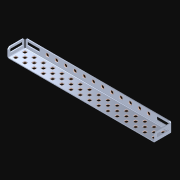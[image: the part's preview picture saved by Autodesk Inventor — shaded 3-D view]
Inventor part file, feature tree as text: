
AUTODESK INVENTOR PART (.ipt)
format: ipt  version: 2021 (Build 250183000, 183)  size: 1,003,520 bytes
history: native  units: in
note: dims shown in document units (in); Inventor stores cm internally (conversion verified against a paired STEP export)
features: other x60, extrude x59, pattern_linear x3, sketch x2, imported_body x1
ambient origin geometry x8: Origin, YZ Plane, XZ Plane, XY Plane, X Axis, Y Axis, Z Axis, Center Point
bodies: Body1 (feature_tree), Body2 (feature_tree), Body3 (feature_tree), Body4 (feature_tree), Body5 (feature_tree), Body6 (feature_tree), Body7 (feature_tree), Body8 (feature_tree), Body9 (feature_tree), Body10 (feature_tree), Body11 (feature_tree), Body12 (feature_tree), Body13 (feature_tree), Body14 (feature_tree), Body15 (feature_tree), Body16 (feature_tree), Body17 (feature_tree), Body18 (feature_tree), Body19 (feature_tree), Body20 (feature_tree), Body21 (feature_tree), Body22 (feature_tree), Body23 (feature_tree), Body24 (feature_tree), Body25 (feature_tree), Body26 (feature_tree), Body27 (feature_tree), Body28 (feature_tree), Body29 (feature_tree), Body30 (feature_tree), Body31 (feature_tree), Body32 (feature_tree), Body33 (feature_tree), Body34 (feature_tree), Body35 (feature_tree), Body36 (feature_tree), Body37 (feature_tree), Body38 (feature_tree), Body39 (feature_tree), Body40 (feature_tree), Body41 (feature_tree), Body42 (feature_tree), Body43 (feature_tree), Body44 (feature_tree), Body45 (feature_tree), Body46 (feature_tree), Body47 (feature_tree), Body48 (feature_tree), Body49 (feature_tree), Body50 (feature_tree), Body51 (feature_tree), Body52 (feature_tree), Body53 (feature_tree), Body54 (feature_tree), Body55 (feature_tree), Body56 (feature_tree), Body57 (feature_tree), Body58 (feature_tree), Body59 (feature_tree), Body60 (feature_tree)
feature tree (125):
  parser-record x1  (decoder bookkeeping rows leaked as tree rows — omitted from the tree; the rows remain in map.json)
  imported_body  "Base1"
  pattern_linear  "Rectangular Pattern1"  Count1=16 Spacing1=0.5in
  pattern_linear  "Rectangular Pattern2"  Count1=2 Spacing1=0.5in
  pattern_linear  "Rectangular Pattern3"  Count1=15 Spacing1=0.5in
  other  "Srf1"
  other  "Srf2"
  other  "Srf3"
  other  "Srf4"
  other  "Srf5"
  other  "Srf6"
  other  "Srf7"
  other  "Srf8"
  other  "Srf9"
  other  "Srf10"
  other  "Srf11"
  other  "Srf12"
  other  "Srf13"
  other  "Srf14"
  other  "Srf15"
  other  "Srf16"
  other  "Srf17"
  other  "Srf18"
  other  "Srf19"
  other  "Srf20"
  other  "Srf21"
  other  "Srf22"
  other  "Srf23"
  other  "Srf24"
  other  "Srf25"
  other  "Srf26"
  other  "Srf27"
  other  "Srf28"
  other  "Srf29"
  other  "Srf30"
  other  "Srf31"
  other  "Srf32"
  sketch  "Sketch10"  dims[d70=0.046in d71=0.0in d72=6.2992in d74=0.5in d75=0.7874in d77=0.5in]
  other  "Srf33"
  other  "Srf34"
  other  "Srf35"
  other  "Srf36"
  other  "Srf37"
  other  "Srf38"
  other  "Srf39"
  other  "Srf40"
  other  "Srf41"
  other  "Srf42"
  other  "Srf43"
  other  "Srf44"
  other  "Srf45"
  other  "Srf46"
  other  "Srf47"
  sketch  "Sketch11"  dims[d79=0.046in d80=0.0in d81=5.9055in d83=0.5in d85=0.046in d86=0.0in d87=4.7244in d89=0.5in d90=0.0in d91=0.0in d92=0.0in d93=0.0in d94=0.0in d95=0.0in d96=0.0in d97=0.0in d98=0.0in d99=0.0in d100=0.0in d101=0.0in d102=0.0in d103=0.0in d104=0.0in d105=0.0in d106=0.0in d107=0.0in d108=0.0in d109=0.0in d110=0.0in d111=0.0in d112=0.0in d113=0.0in d114=0.0in d115=0.0in d116=0.0in d117=0.0in d118=0.0in d119=0.0in d120=0.0in d121=0.0in d122=0.0in d123=0.0in d124=0.0in d125=0.0in d126=0.0in d127=0.0in d128=0.0in d129=0.0in d130=0.0in d131=0.0in d132=0.0in d133=0.0in d134=0.0in d135=0.0in d136=0.0in d137=0.0in d138=0.0in d139=0.0in d140=0.0in d141=0.0in d142=0.0in d143=0.0in d144=0.0in d145=0.0in d146=0.0in d147=0.0in d148=0.0in d149=0.0in d150=0.0in d151=0.0in d152=0.0in d153=0.0in d154=0.0in d155=0.0in d156=0.0in d157=0.0in d158=0.0in d159=0.0in d160=0.0in d161=0.0in d162=0.0in d163=0.0in d164=0.0in d165=0.0in d166=0.0in d167=0.0in d168=0.0in d169=0.0in d170=0.0in d171=0.0in d172=0.0in d173=0.0in d174=0.0in d175=0.0in d176=0.0in d177=0.0in d178=0.0in d179=0.0in d180=0.0in d181=0.0in d182=0.0in d183=0.0in d184=0.0in d185=0.0in d186=0.0in d187=0.0in d188=0.0in d189=0.0in d190=0.0in d191=0.0in d192=0.0in d193=0.0in d194=0.0in d195=0.0in d196=0.0in d197=0.0in d198=0.0in d199=0.0in d200=0.0in d201=0.0in d202=0.0in d203=0.0in d204=0.0in d205=0.0in d206=0.0in d207=0.0in]
  other  "Srf48"
  other  "Srf49"
  other  "Srf50"
  other  "Srf51"
  other  "Srf52"
  other  "Srf53"
  other  "Srf54"
  other  "Srf55"
  other  "Srf56"
  other  "Srf57"
  other  "Srf58"
  other  "Srf59"
  extrude  "ExtrusionSrf1"  Depth=0.046in TaperAngle=0.0deg
  extrude  "ExtrusionSrf33"  Depth=0.5in
  extrude  "ExtrusionSrf48"  [1 undecoded]
  extrude  "ExtrusionSrf2"  [1 undecoded]
  extrude  "ExtrusionSrf3"  [1 undecoded]
  extrude  "ExtrusionSrf4"  [1 undecoded]
  extrude  "ExtrusionSrf5"  [1 undecoded]
  extrude  "ExtrusionSrf6"  [1 undecoded]
  extrude  "ExtrusionSrf7"  [1 undecoded]
  extrude  "ExtrusionSrf8"  [1 undecoded]
  extrude  "ExtrusionSrf9"  [1 undecoded]
  extrude  "ExtrusionSrf10"  [1 undecoded]
  extrude  "ExtrusionSrf11"  [1 undecoded]
  extrude  "ExtrusionSrf12"  [1 undecoded]
  extrude  "ExtrusionSrf13"  [1 undecoded]
  extrude  "ExtrusionSrf14"  [1 undecoded]
  extrude  "ExtrusionSrf15"  [1 undecoded]
  extrude  "ExtrusionSrf16"  [1 undecoded]
  extrude  "ExtrusionSrf17"  [1 undecoded]
  extrude  "ExtrusionSrf18"  [1 undecoded]
  extrude  "ExtrusionSrf19"  [1 undecoded]
  extrude  "ExtrusionSrf20"  [1 undecoded]
  extrude  "ExtrusionSrf21"  [1 undecoded]
  extrude  "ExtrusionSrf22"  [1 undecoded]
  extrude  "ExtrusionSrf23"  [1 undecoded]
  extrude  "ExtrusionSrf24"  [1 undecoded]
  extrude  "ExtrusionSrf25"  [1 undecoded]
  extrude  "ExtrusionSrf26"  [1 undecoded]
  extrude  "ExtrusionSrf27"  [1 undecoded]
  extrude  "ExtrusionSrf28"  [1 undecoded]
  extrude  "ExtrusionSrf29"  [1 undecoded]
  extrude  "ExtrusionSrf30"  [1 undecoded]
  extrude  "ExtrusionSrf31"  [1 undecoded]
  extrude  "ExtrusionSrf32"  [1 undecoded]
  extrude  "ExtrusionSrf34"  [1 undecoded]
  extrude  "ExtrusionSrf35"  [1 undecoded]
  extrude  "ExtrusionSrf36"  [1 undecoded]
  extrude  "ExtrusionSrf37"  [1 undecoded]
  extrude  "ExtrusionSrf38"  [1 undecoded]
  extrude  "ExtrusionSrf39"  [1 undecoded]
  extrude  "ExtrusionSrf40"  [1 undecoded]
  extrude  "ExtrusionSrf41"  [1 undecoded]
  extrude  "ExtrusionSrf42"  [1 undecoded]
  extrude  "ExtrusionSrf43"  [1 undecoded]
  extrude  "ExtrusionSrf44"  [1 undecoded]
  extrude  "ExtrusionSrf45"  [1 undecoded]
  extrude  "ExtrusionSrf46"  [1 undecoded]
  extrude  "ExtrusionSrf47"  [1 undecoded]
  extrude  "ExtrusionSrf49"  [1 undecoded]
  extrude  "ExtrusionSrf50"  [1 undecoded]
  extrude  "ExtrusionSrf51"  [1 undecoded]
  extrude  "ExtrusionSrf52"  [1 undecoded]
  extrude  "ExtrusionSrf53"  [1 undecoded]
  extrude  "ExtrusionSrf54"  [1 undecoded]
  extrude  "ExtrusionSrf55"  [1 undecoded]
  extrude  "ExtrusionSrf56"  [1 undecoded]
  extrude  "ExtrusionSrf57"  [1 undecoded]
  extrude  "ExtrusionSrf58"  [1 undecoded]
  extrude  "ExtrusionSrf59"  [1 undecoded]
note: 57 required parameter values undecoded (feature->parameter linkage not recoverable at this tier; creation-order binding heuristic only, values carry confidence <= 0.55)
